# Revit family: IlluminatedMirror-WithCeramicFrame-Vitra-LiquidSeries-66743
name_source: partatom
category: Furniture Systems
revit_build: Autodesk Revit 2017 (Build: 20160225_1515(x64)
units: mm (PartAtom-declared; Revit-internal decimal feet)

## family parameters
Cut with Voids When Loaded = No
Host = Face
OmniClass Number = 23.40.00.00
OmniClass Title = Equipment and Furnishings
Part Type = Normal
Room Calculation Point = No
Round Connector Dimension = Use Diameter
Shared = Yes

## types (1)
- IlluminatedMirror-WithCeramicFrame-Vitra-LiquidSeries-66743
    Article No. (default) = 66743
    BIMobject category = Mirrors
    Brand = VitrA
    Color = Mirror
    Default Elevation = 1200 mm
    Description = Liquid Illuminated Mirror - With Ceramic Frame - 50x80cm - Wired to Room Lighting
    Design country = Turkey
    IFC Classification = Furniture
    Main Material = Glass
    Manufacturer = Vitra
    Manufacturer name = Vitra
    Masterformat 2014 Code = 08 83 00
    Masterformat 2014 Description = Mirrors
    Model = 66743
    Mounting type = Wall Hung
    Nominal Depth (mm) = 65 mm  [stored 0.213255 ft]
    Nominal Height (mm) = 800 mm
    Nominal Width (mm) = 500 mm  [stored 1.64042 ft]
    OmniClass Code = 23-21 00 00
    OmniClass Description = Furnishings, Fixtures and Equipment Products
    Primary Material = Mirror
    Product SKU = 66743
    Product certification = https://www.vitraglobal.com
    Product family = Liquid
    Product group = Mirror
    Product url = https://www.vitraglobal.com
    Secondary Material = White (Ceramic)
    Technical description = https://www.vitraglobal.com
    UNSPSC Description = Mirrors
    URL = https://vitraglobal.com
    Uniclass 1.4 Code = L8732
    Uniclass 1.4 Description = Mirrors
    Uniclass 2.0 Code = PR-71-55
    Uniclass 2.0 Description = Mirrors
    Uniclass 2015 Code = Pr_25_71_53
    Uniclass 2015 Name = Mirrors
    Uniformat II Code = E20
    Uniformat II Description = FURNISHINGS
    Warranty Period (Year) = 2
    Youtube = https://www.youtube.com

note: [stored X ft] marks values corroborated as IEEE doubles in the binary element streams (Revit-internal decimal feet)

## geometry (parser evidence)
native form markers: Sweep x1
no freeform markers — native parametric forms only
